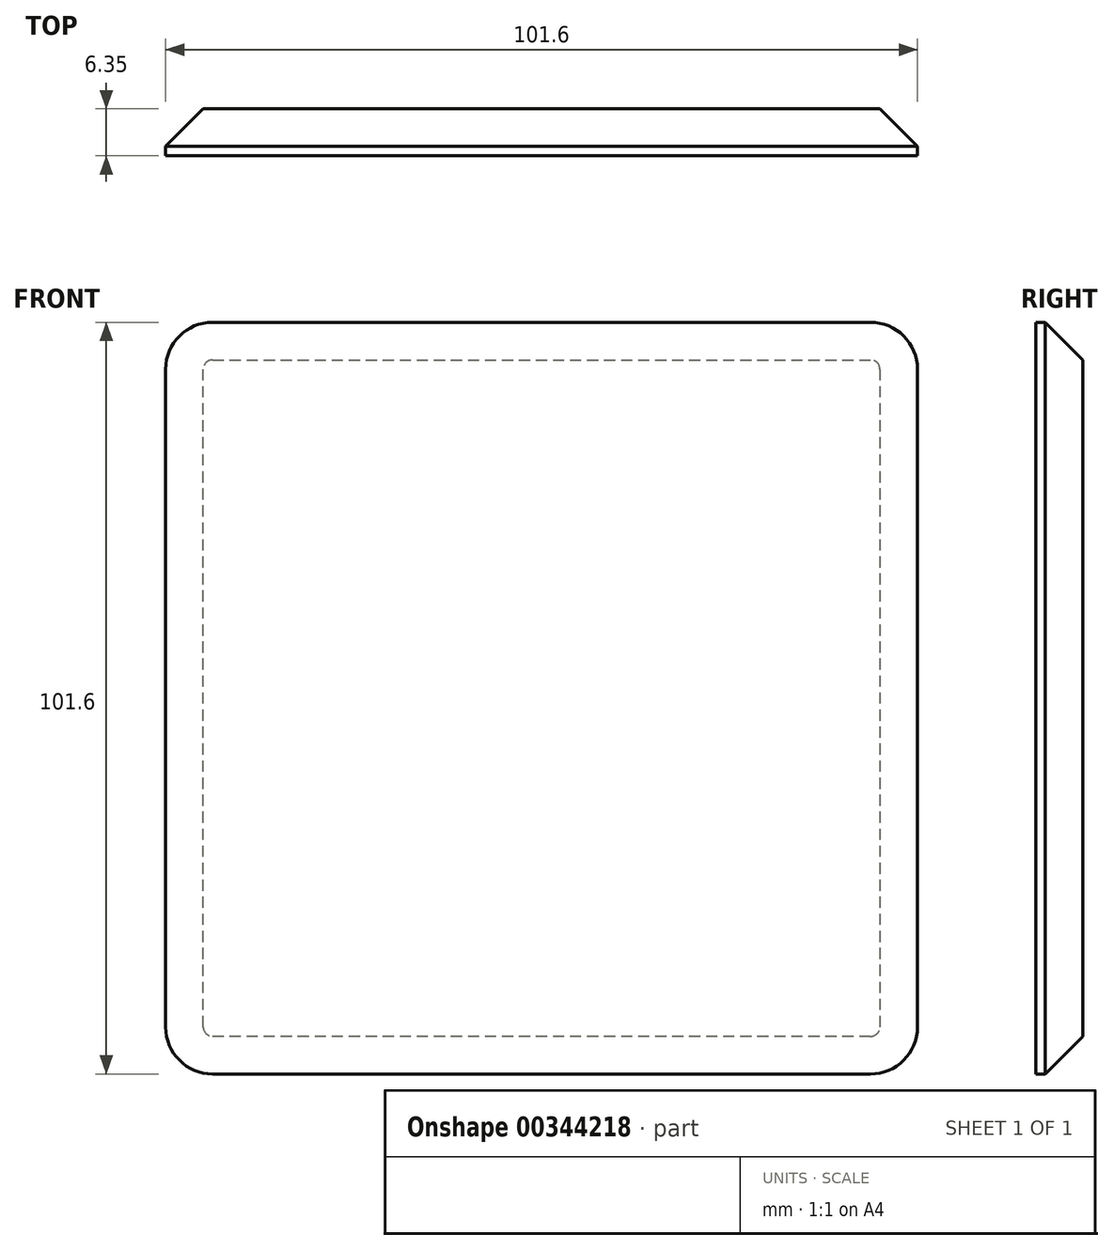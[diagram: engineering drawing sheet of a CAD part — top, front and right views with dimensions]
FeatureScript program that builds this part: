
annotation { "Feature Type Name" : "Feature", "Feature Type Description" : "" }
export const myFeature = defineFeature(function(context is Context, id is Id, definition is map)
    precondition{}
    {
        {
            var Q0;
            Q0=qCreatedBy(makeId("Front.planeOp"),FACE);
            var sketch = newSketch(context, id + "F0", { "sketchPlane" : qUnion([Q0])});
            skLineSegment(sketch, "E0.bottom", {"start": v(44.45, 50.8) * mm, "end": v(-44.45, 50.8) * mm});
            skLineSegment(sketch, "E0.top", {"start": v(44.45, -50.8) * mm, "end": v(-44.45, -50.8) * mm});
            skLineSegment(sketch, "E0.left", {"start": v(50.8, 44.45) * mm, "end": v(50.8, -44.45) * mm});
            skLineSegment(sketch, "E0.right", {"start": v(-50.8, 44.45) * mm, "end": v(-50.8, -44.45) * mm});
            skPoint(sketch, "E0.middle", {"position": v(0, 0) * mm});
            skPoint(sketch, "E1.visualSharp", {"position": v(50.8, 50.8) * mm});
            skArc(sketch, "E1.filletArc", {"start": v(50.8, 44.45) * mm, "mid": v(48.94, 48.94) * mm, "end": v(44.45, 50.8) * mm});
            skPoint(sketch, "E2.visualSharp", {"position": v(50.8, -50.8) * mm});
            skArc(sketch, "E2.filletArc", {"start": v(44.45, -50.8) * mm, "mid": v(48.94, -48.94) * mm, "end": v(50.8, -44.45) * mm});
            skPoint(sketch, "E3.visualSharp", {"position": v(-50.8, -50.8) * mm});
            skArc(sketch, "E3.filletArc", {"start": v(-50.8, -44.45) * mm, "mid": v(-48.94, -48.94) * mm, "end": v(-44.45, -50.8) * mm});
            skPoint(sketch, "E4.visualSharp", {"position": v(-50.8, 50.8) * mm});
            skArc(sketch, "E4.filletArc", {"start": v(-44.45, 50.8) * mm, "mid": v(-48.94, 48.94) * mm, "end": v(-50.8, 44.45) * mm});
            skSolve(sketch);
        }
        {
            var Q0;
            Q0 = qSketchRegion(id + "F0", true);
            extrude(context, id + "F1", {"entities" : qUnion([Q0]), "depth" : 6.35 * mm});
        }
        {
            var Q0;
            Q0=makeQuery(id+"F1.opExtrude","CAP_EDGE",EDGE,{"disambiguationData":[OSD([sQuery(id+"F0.wireOp",EDGE,"E0.bottom")])],"isStart":true});
            chamfer(context, id + "F2", {"entities" : qUnion([Q0]), "width" : 5.08 * mm, "tangentPropagation" : true});
        }
    });
